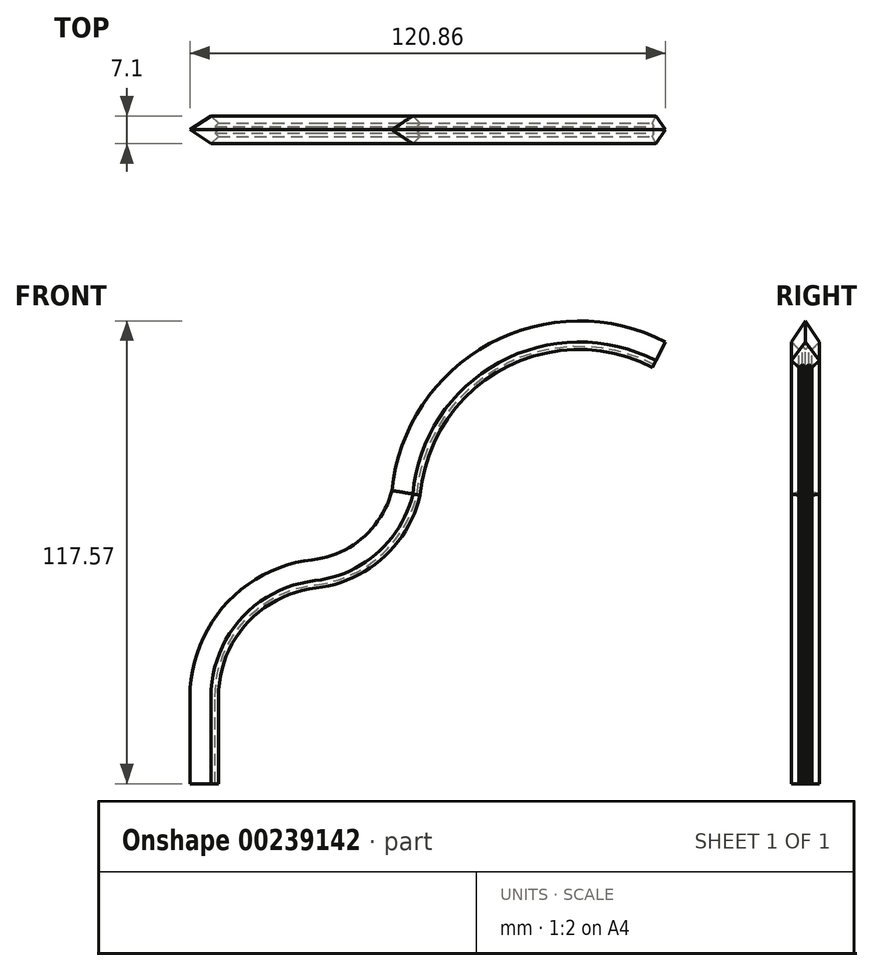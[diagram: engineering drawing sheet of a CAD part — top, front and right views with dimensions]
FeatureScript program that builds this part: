
annotation { "Feature Type Name" : "Feature", "Feature Type Description" : "" }
export const myFeature = defineFeature(function(context is Context, id is Id, definition is map)
    precondition{}
    {
        {
            var Q0;
            Q0=qCreatedBy(makeId("Front.planeOp"),FACE);
            var sketch = newSketch(context, id + "F0", { "sketchPlane" : qUnion([Q0])});
            skLineSegment(sketch, "E0", {"start": v(0, 0) * mm, "end": v(0, 22.05) * mm});
            skArc(sketch, "E1", {"start": v(26.45, 51.58) * mm, "mid": v(7.58, 41.87) * mm, "end": v(0, 22.05) * mm});
            skArc(sketch, "E2", {"start": v(26.45, 51.58) * mm, "mid": v(42.33, 58.68) * mm, "end": v(51.27, 73.6) * mm});
            skArc(sketch, "E3", {"start": v(113.04, 107.46) * mm, "mid": v(73.14, 106.98) * mm, "end": v(51.27, 73.6) * mm});
            skSolve(sketch);
        }
        {
            var Q0;
            Q0=qCreatedBy(makeId("Top.planeOp"),FACE);
            var sketch = newSketch(context, id + "F1", { "sketchPlane" : qUnion([Q0])});
            skLineSegment(sketch, "E4", {"start": v(0, 3.55) * mm, "end": v(-5.36, 0) * mm});
            skLineSegment(sketch, "E5", {"start": v(-5.36, 0) * mm, "end": v(0, -3.55) * mm});
            skLineSegment(sketch, "E6", {"start": v(0, -3.55) * mm, "end": v(1.89, -1.66) * mm});
            skLineSegment(sketch, "E7", {"start": v(1.89, -1.66) * mm, "end": v(1.05, -0.83) * mm});
            skLineSegment(sketch, "E8", {"start": v(1.05, -0.83) * mm, "end": v(1.89, 0) * mm});
            skLineSegment(sketch, "E9", {"start": v(1.89, 0) * mm, "end": v(1.05, 0.83) * mm});
            skLineSegment(sketch, "E10", {"start": v(1.05, 0.83) * mm, "end": v(1.89, 1.66) * mm});
            skLineSegment(sketch, "E11", {"start": v(1.89, 1.66) * mm, "end": v(0, 3.55) * mm});
            skSolve(sketch);
        }
        {
            var Q0;
            Q0 = qSketchRegion(id + "F1", true);
            var Q1;
            Q1 = qConstructionFilter(qBodyType(qCreatedBy(id + "F0" ,EDGE), BodyType.WIRE), ConstructionObject.NO);
            sweep(context, id + "F2", {"profiles" : qUnion([Q0]), "path" : qUnion([Q1])});
        }
    });
